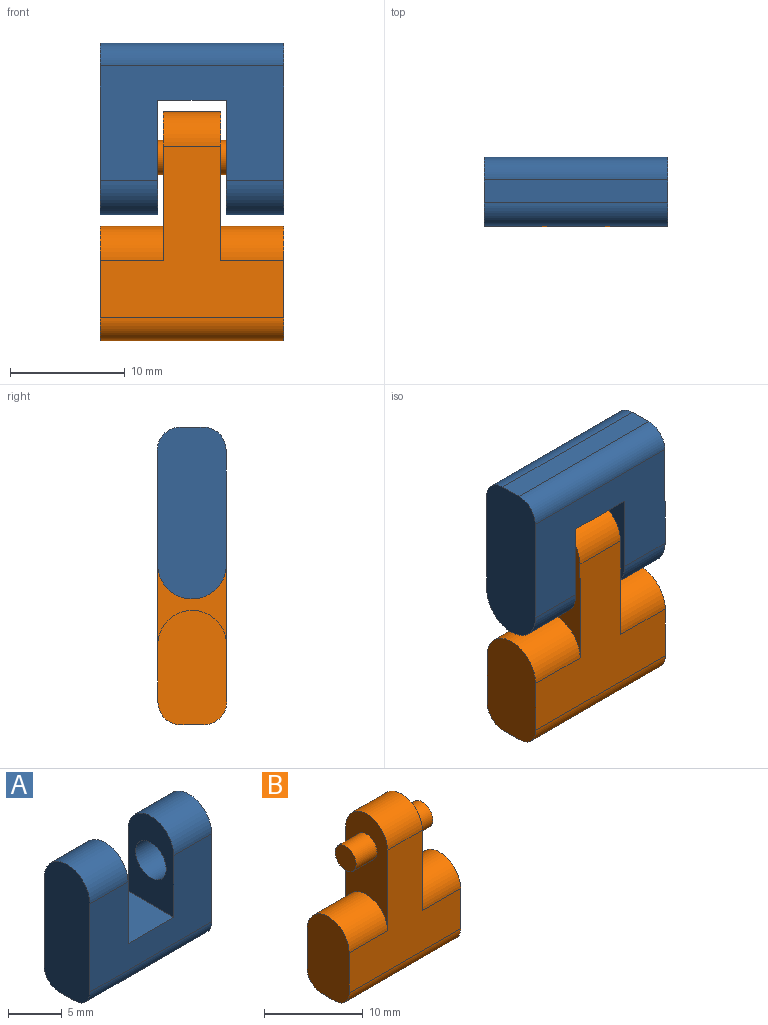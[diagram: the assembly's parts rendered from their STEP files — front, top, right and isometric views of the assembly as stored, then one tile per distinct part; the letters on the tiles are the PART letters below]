
ASSEMBLY  parts=2 mates=1
PART A: 16 faces, bbox 16x6x15 mm
  f0: plane 10x6mm, normal (1,0,0), area 43.6mm2, adj f5,f6,f7,f10,f13
  f1: plane 15x6mm, normal (-1,0,0), area 84.4mm2, adj f2,f6,f7,f13,f14,f15
  f2: plane 16x2mm, normal (0,0,-1), area 32mm2, adj f1,f3,f14,f15
  f3: plane 15x6mm, normal (1,0,0), area 84.4mm2, adj f2,f6,f7,f12,f14,f15
  f4: plane 10x6mm, normal (-1,0,0), area 43.6mm2, adj f5,f6,f7,f9,f12
  f5: plane 6x6mm, normal (0,0,1), area 36mm2, adj f0,f4,f6,f7
  f6: plane 16x10mm, normal (0,-1,0), area 118mm2, adj f0,f1,f3,f4,f5,f12,f13,f15
  f7: plane 16x10mm, normal (0,1,0), area 118mm2, adj f0,f1,f3,f4,f5,f12,f13,f14
  f8: plane 4x4mm, normal (-1,0,0), area 12.6mm2, adj f9
  f9: cylinder r=2mm len=4mm, axis (1,0,0), area 50.3mm2, adj f4,f8
  f10: cylinder r=2mm len=4mm, axis (1,0,0), area 50.3mm2, adj f0,f11
  f11: plane 4x4mm, normal (1,0,0), area 12.6mm2, adj f10
  f12: cylinder r=3mm len=6mm, axis (1,0,0), area 47.1mm2, adj f3,f4,f6,f7
  f13: cylinder r=3mm len=6mm, axis (1,0,0), area 47.1mm2, adj f0,f1,f6,f7
  f14: cylinder r=2mm len=16mm, axis (1,0,0), area 50.3mm2, adj f1,f2,f3,f7
  f15: cylinder r=2mm len=16mm, axis (-1,0,0), area 50.3mm2, adj f1,f2,f3,f6
PART B: 16 faces, bbox 16x6x20 mm
  f0: plane 13x6mm, normal (-1,0,0), area 52.9mm2, adj f5,f6,f9,f11,f13
  f1: plane 10x6mm, normal (-1,0,0), area 54.4mm2, adj f2,f5,f6,f13,f14,f15
  f2: plane 16x2mm, normal (0,0,-1), area 32mm2, adj f1,f3,f14,f15
  f3: plane 10x6mm, normal (1,0,0), area 54.4mm2, adj f2,f5,f6,f12,f14,f15
  f4: plane 13x6mm, normal (1,0,0), area 52.9mm2, adj f5,f6,f8,f11,f12
  f5: plane 16x15mm, normal (0,-1,0), area 130mm2, adj f0,f1,f3,f4,f11,f12,f13,f15
  f6: plane 16x15mm, normal (0,1,0), area 130mm2, adj f0,f1,f3,f4,f11,f12,f13,f14
  f7: plane 3x3mm, normal (1,0,0), area 7.1mm2, adj f8
  f8: cylinder r=1.5mm len=3mm, axis (-1,0,0), area 28.3mm2, adj f4,f7
  f9: cylinder r=1.5mm len=3mm, axis (-1,0,0), area 28.3mm2, adj f0,f10
  f10: plane 3x3mm, normal (-1,0,0), area 7.1mm2, adj f9
  f11: cylinder r=3mm len=6mm, axis (1,0,0), area 47.1mm2, adj f0,f4,f5,f6
  f12: cylinder r=3mm len=6mm, axis (1,0,0), area 51.8mm2, adj f3,f4,f5,f6
  f13: cylinder r=3mm len=6mm, axis (1,0,0), area 51.8mm2, adj f0,f1,f5,f6
  f14: cylinder r=2mm len=16mm, axis (1,0,0), area 50.3mm2, adj f1,f2,f3,f6
  f15: cylinder r=2mm len=16mm, axis (-1,0,0), area 50.3mm2, adj f1,f2,f3,f5
PLACE A rot(axis=(1,0,0),179.9deg) t=(-27.63,-17.64,1.76)mm
PLACE B rot(axis=(-1,0,0),0.1deg) t=(-27.63,-11.64,0.74)mm
MATE revolute A.f9 <-> B.f8  axis (1,0,0) through (-22.63,-14.62,6.75)mm
